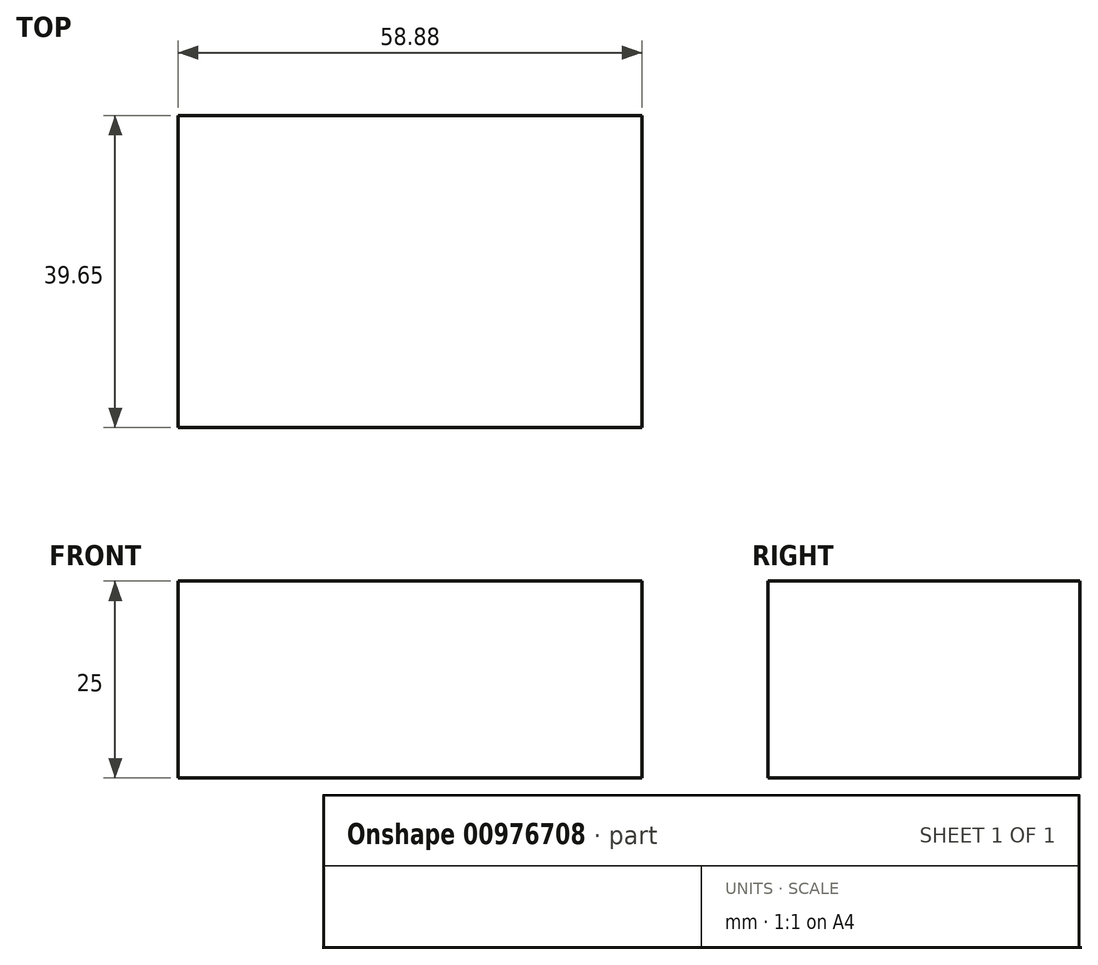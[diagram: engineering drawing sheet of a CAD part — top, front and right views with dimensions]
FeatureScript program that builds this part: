
annotation { "Feature Type Name" : "Feature", "Feature Type Description" : "" }
export const myFeature = defineFeature(function(context is Context, id is Id, definition is map)
    precondition{}
    {
        {
            var Q0;
            Q0=qCreatedBy(makeId("Top.planeOp"),FACE);
            var sketch = newSketch(context, id + "F0", { "sketchPlane" : qUnion([Q0])});
            skLineSegment(sketch, "E0.bottom", {"start": v(0, 0) * mm, "end": v(58.88, 0) * mm});
            skLineSegment(sketch, "E0.top", {"start": v(0, 39.65) * mm, "end": v(58.88, 39.65) * mm});
            skLineSegment(sketch, "E0.left", {"start": v(0, 0) * mm, "end": v(0, 39.65) * mm});
            skLineSegment(sketch, "E0.right", {"start": v(58.88, 0) * mm, "end": v(58.88, 39.65) * mm});
            skSolve(sketch);
        }
        {
            var Q0;
            Q0 = qSketchRegion(id + "F0", true);
            extrude(context, id + "F1", {"entities" : qUnion([Q0]), "depth" : 25 * mm, "offsetDistance" : 25 * mm});
        }
    });
